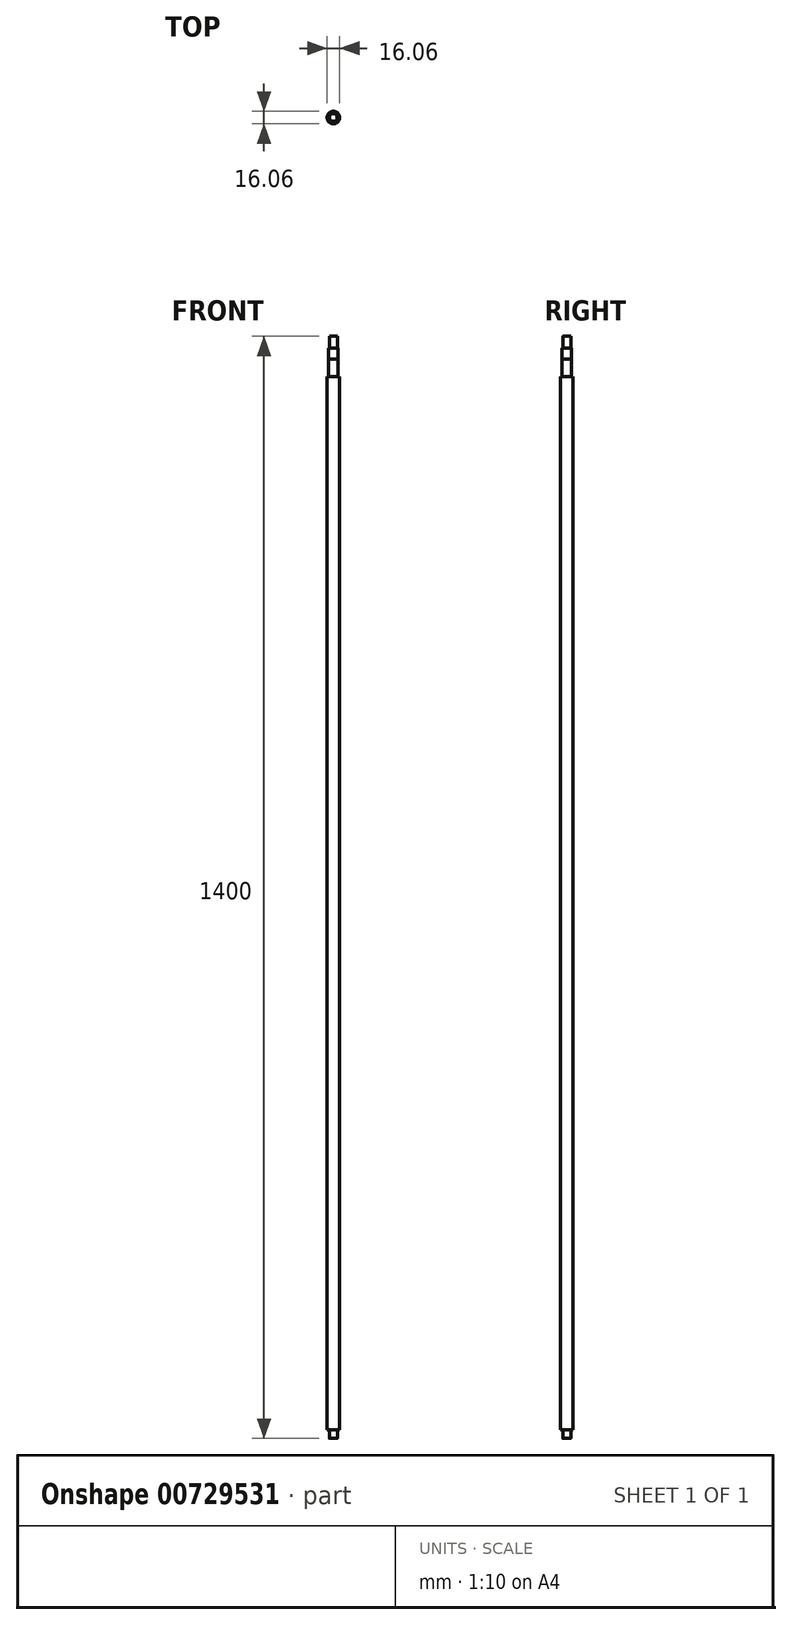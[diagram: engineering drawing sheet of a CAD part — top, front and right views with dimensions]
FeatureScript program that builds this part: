
annotation { "Feature Type Name" : "Feature", "Feature Type Description" : "" }
export const myFeature = defineFeature(function(context is Context, id is Id, definition is map)
    precondition{}
    {
        {
            var Q0;
            Q0=qCreatedBy(makeId("Front.planeOp"),FACE);
            var sketch = newSketch(context, id + "F0", { "sketchPlane" : qUnion([Q0])});
            skLineSegment(sketch, "E0", {"start": v(0, 59.37) * mm, "end": v(0, -680) * mm});
            skLineSegment(sketch, "E1.bottom", {"start": v(-8.02, 669) * mm, "end": v(8.03, 669) * mm});
            skLineSegment(sketch, "E1.top", {"start": v(-8.02, -669) * mm, "end": v(8.03, -669) * mm});
            skLineSegment(sketch, "E1.left", {"start": v(-8.03, 669) * mm, "end": v(-8.02, -669) * mm});
            skLineSegment(sketch, "E1.right", {"start": v(8.02, 669) * mm, "end": v(8.03, -669) * mm});
            skPoint(sketch, "E1.middle", {"position": v(0, 0) * mm});
            skLineSegment(sketch, "E2.bottom", {"start": v(6, 669) * mm, "end": v(-6, 669) * mm});
            skLineSegment(sketch, "E2.top", {"start": v(6, 691) * mm, "end": v(-6, 691) * mm});
            skLineSegment(sketch, "E2.left", {"start": v(6, 669) * mm, "end": v(6, 691) * mm});
            skLineSegment(sketch, "E2.right", {"start": v(-6, 669) * mm, "end": v(-6, 691) * mm});
            skPoint(sketch, "E2.middle", {"position": v(0, 680) * mm});
            skLineSegment(sketch, "E3.bottom", {"start": v(5, -669) * mm, "end": v(-5, -669) * mm});
            skLineSegment(sketch, "E3.top", {"start": v(5, -680) * mm, "end": v(-5, -680) * mm});
            skLineSegment(sketch, "E3.left", {"start": v(5, -669) * mm, "end": v(5, -680) * mm});
            skLineSegment(sketch, "E3.right", {"start": v(-5, -669) * mm, "end": v(-5, -680) * mm});
            skPoint(sketch, "E3.middle", {"position": v(0, -674.5) * mm});
            skLineSegment(sketch, "E4.top", {"start": v(6, 705) * mm, "end": v(-6, 705) * mm});
            skLineSegment(sketch, "E4.left", {"start": v(6, 691) * mm, "end": v(6, 705) * mm});
            skLineSegment(sketch, "E4.right", {"start": v(-6, 691) * mm, "end": v(-6, 705) * mm});
            skPoint(sketch, "E4.middle", {"position": v(0, 698) * mm});
            skLineSegment(sketch, "E5.bottom", {"start": v(5, 705) * mm, "end": v(-5, 705) * mm});
            skLineSegment(sketch, "E5.top", {"start": v(5, 720) * mm, "end": v(-5, 720) * mm});
            skLineSegment(sketch, "E5.left", {"start": v(5, 705) * mm, "end": v(5, 720) * mm});
            skLineSegment(sketch, "E5.right", {"start": v(-5, 705) * mm, "end": v(-5, 720) * mm});
            skPoint(sketch, "E5.middle", {"position": v(0, 712.5) * mm});
            skLineSegment(sketch, "E6", {"start": v(0, 59.37) * mm, "end": v(0, 720) * mm});
            skSolve(sketch);
        }
        {
            var Q0;
            {var subQ3=sQuery(id+"F0.wireOp",EDGE,"E5.left");Q0=makeQuery(id+"F0.imprint","IMPRINT",FACE,{"disambiguationData":[TD([[makeQuery(id+"F0.imprint","IMPRINT",EDGE,{"derivedFrom":subQ3}),1.0]])]});}
            var Q1;
            {var subQ0=sQuery(id+"F0.wireOp",EDGE,"E2.left");Q1=makeQuery(id+"F0.imprint","IMPRINT",FACE,{"disambiguationData":[TD([[makeQuery(id+"F0.imprint","IMPRINT",EDGE,{"derivedFrom":subQ0}),1.0]])]});}
            var Q2;
            {var subQ8=sQuery(id+"F0.wireOp",EDGE,"E1.right");Q2=makeQuery(id+"F0.imprint","IMPRINT",FACE,{"disambiguationData":[TD([[makeQuery(id+"F0.imprint","IMPRINT",EDGE,{"derivedFrom":subQ8}),-1.0]])]});}
            var Q3;
            {var subQ5=sQuery(id+"F0.wireOp",EDGE,"E3.left");Q3=makeQuery(id+"F0.imprint","IMPRINT",FACE,{"disambiguationData":[TD([[makeQuery(id+"F0.imprint","IMPRINT",EDGE,{"derivedFrom":subQ5}),-1.0]])]});}
            var Q4;
            Q4=sQuery(id+"F0.wireOp",EDGE,"E0");
            revolve(context, id + "F1", {"surfaceOperationType" : NewSurfaceOperationType.NEW, "entities" : qUnion([Q0, Q1, Q2, Q3]), "axis" : qUnion([Q4]), "revolveType" : RevolveType.FULL});
        }
        {
            var Q0;
            {var subQ0=sQuery(id+"F0.wireOp",EDGE,"E4.left");Q0=makeQuery(id+"F0.imprint","IMPRINT",FACE,{"disambiguationData":[TD([[makeQuery(id+"F0.imprint","IMPRINT",EDGE,{"derivedFrom":subQ0}),1.0]])]});}
            var Q1;
            Q1=sQuery(id+"F0.wireOp",EDGE,"E6");
            revolve(context, id + "F2", {"surfaceOperationType" : NewSurfaceOperationType.NEW, "entities" : qUnion([Q0]), "axis" : qUnion([Q1]), "revolveType" : RevolveType.FULL});
        }
        {
            var Q0;
            Q0=makeQuery(id+"F1.opRevolve","SWEPT_EDGE",EDGE,{"disambiguationData":[OSD([sQuery(id+"F0.wireOp",EDGE,"E3.top"),sQuery(id+"F0.wireOp",EDGE,"E3.left")])]});
            fillet(context, id + "F3", {"entities" : qUnion([Q0]), "radius" : 0.2 * mm, "tangentPropagation" : true, "allowEdgeOverflow" : false});
        }
        {
            var Q0;
            Q0=sQuery(id+"F0.wireOp",EDGE,"E4.left");
            var Q1;
            Q1=sQuery(id+"F0.wireOp",EDGE,"E6");
            revolve(context, id + "F4", {"bodyType" : ToolBodyType.SURFACE, "surfaceOperationType" : NewSurfaceOperationType.NEW, "surfaceEntities" : qUnion([Q0]), "axis" : qUnion([Q1]), "revolveType" : RevolveType.FULL});
        }
    });
